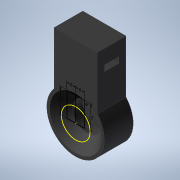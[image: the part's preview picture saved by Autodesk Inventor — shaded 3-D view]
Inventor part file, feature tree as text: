
AUTODESK INVENTOR PART (.ipt)
format: ipt  version: 2022 (Build 260153000, 153)  size: 202,240 bytes
history: native  units: in
note: dims shown in document units (in); Inventor stores cm internally (conversion verified against a paired STEP export)
features: sketch x9, extrude x7, chamfer x1
ambient origin geometry x8: Origin, YZ Plane, XZ Plane, XY Plane, X Axis, Y Axis, Z Axis, Center Point
bodies: Solid1 (feature_tree)
feature tree (17):
  extrude  "Extrusion1"  Depth=0.7874in
  extrude  "Extrusion2"  Depth=1.1811in
  sketch  "Sketch3"  dims[d4=0.7874in d5=0.0in d6=0.7874in]
  extrude  "Extrusion3"  Depth=0.7874in
  sketch  "Sketch5"  dims[d10=0.6693in d11=0.2362in]
  extrude  "Extrusion4"  Depth=0.2362in
  extrude  "Extrusion5"  Depth=0.2362in
  extrude  "Extrusion6"  Depth=0.2362in
  extrude  "Extrusion7"  Depth=0.2362in
  chamfer  "Chamfer1"  Distance=0.9055in
  sketch  "Sketch1"  dims[d0=0.7874in d1=1.5748in]
  sketch  "Sketch2"  dims[d2=1.1811in d3=1.9685in]
  sketch  "Sketch4"  dims[d7=0.5906in d8=0.0in d9=0.2362in]
  sketch  "Sketch6"  dims[d12=0.6693in d13=0.2362in]
  sketch  "Sketch7"  dims[d14=0.9843in d15=0.2362in]
  sketch  "Sketch8"  dims[d16=0.9055in d17=0.9055in d18=0.0in]
  sketch  "Sketch9"  dims[d19=0.4724in d20=0.189in d21=0.189in d22=0.6299in d23=0.0in d24=0.0984in d25=0.0591in d26=0.0984in d27=0.0591in d28=0.315in d29=0.0in d30=0.3937in d31=0.315in d32=0.1969in d33=0.1969in d34=0.6225in d35=0.0in d36=0.0787in d37=0.1181in d38=0.1181in d39=0.1181in d40=0.315in d41=0.0in d42=0.315in d43=0.0787in d44=45.0deg]
